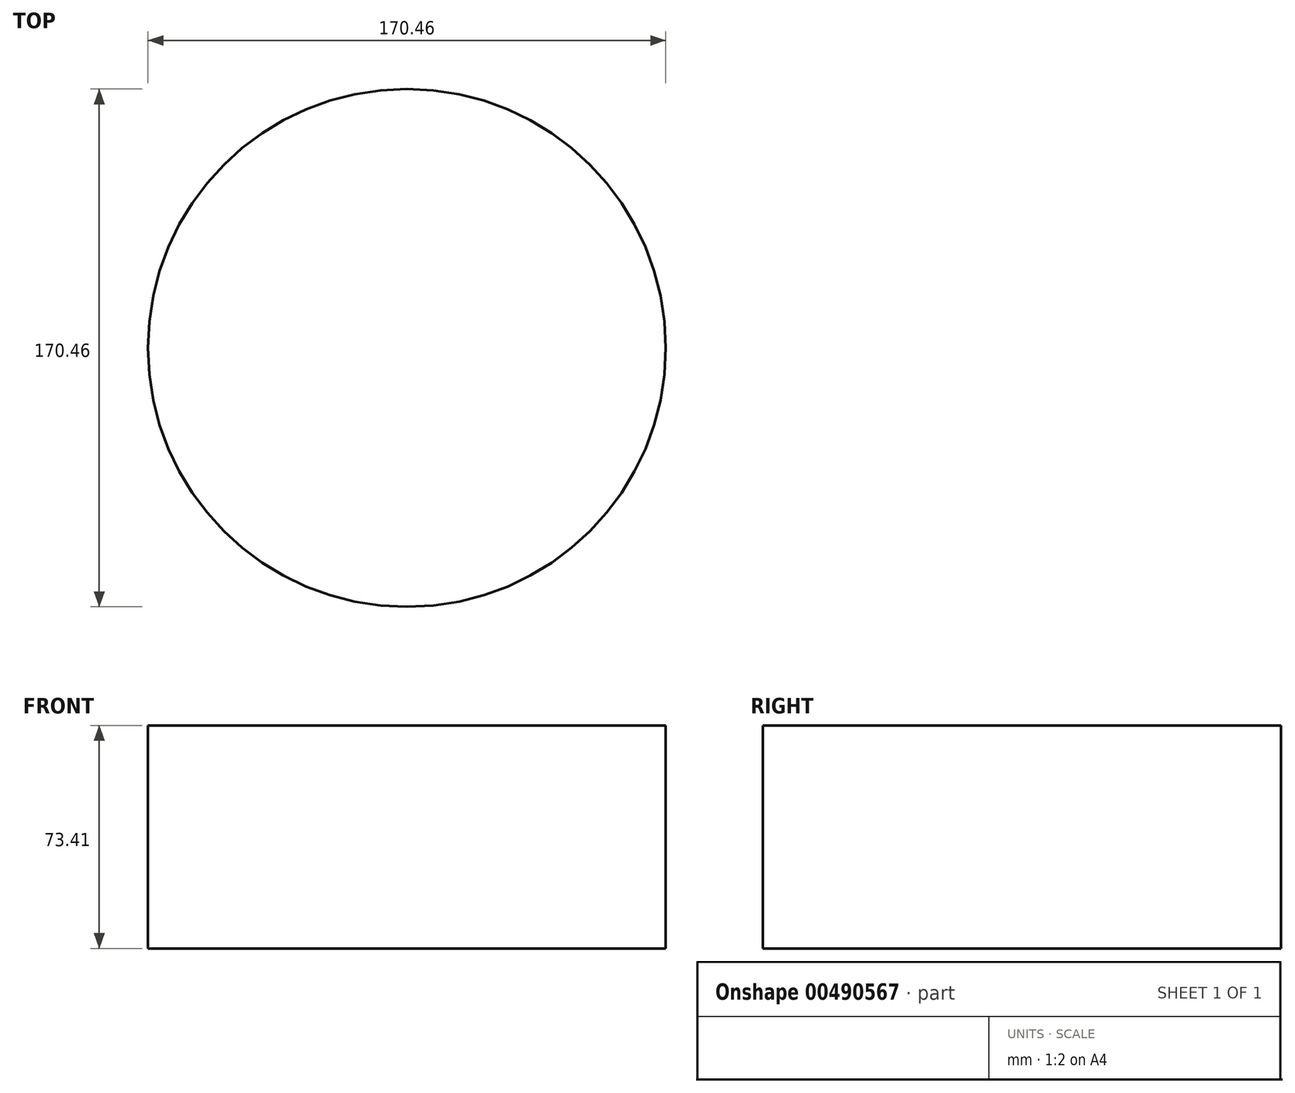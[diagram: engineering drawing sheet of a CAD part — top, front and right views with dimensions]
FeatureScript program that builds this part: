
annotation { "Feature Type Name" : "Feature", "Feature Type Description" : "" }
export const myFeature = defineFeature(function(context is Context, id is Id, definition is map)
    precondition{}
    {
        {
            var Q0;
            Q0=qCreatedBy(makeId("Top.planeOp"),FACE);
            var sketch = newSketch(context, id + "F0", { "sketchPlane" : qUnion([Q0])});
            skCircle(sketch, "E0", {"center": v(0, -29.48) * mm, "radius": 85.23 * mm});
            skSolve(sketch);
        }
        {
            var Q0;
            Q0 = qSketchRegion(id + "F0", true);
            extrude(context, id + "F1", {"entities" : qUnion([Q0]), "depth" : 73.4 * mm});
        }
    });
